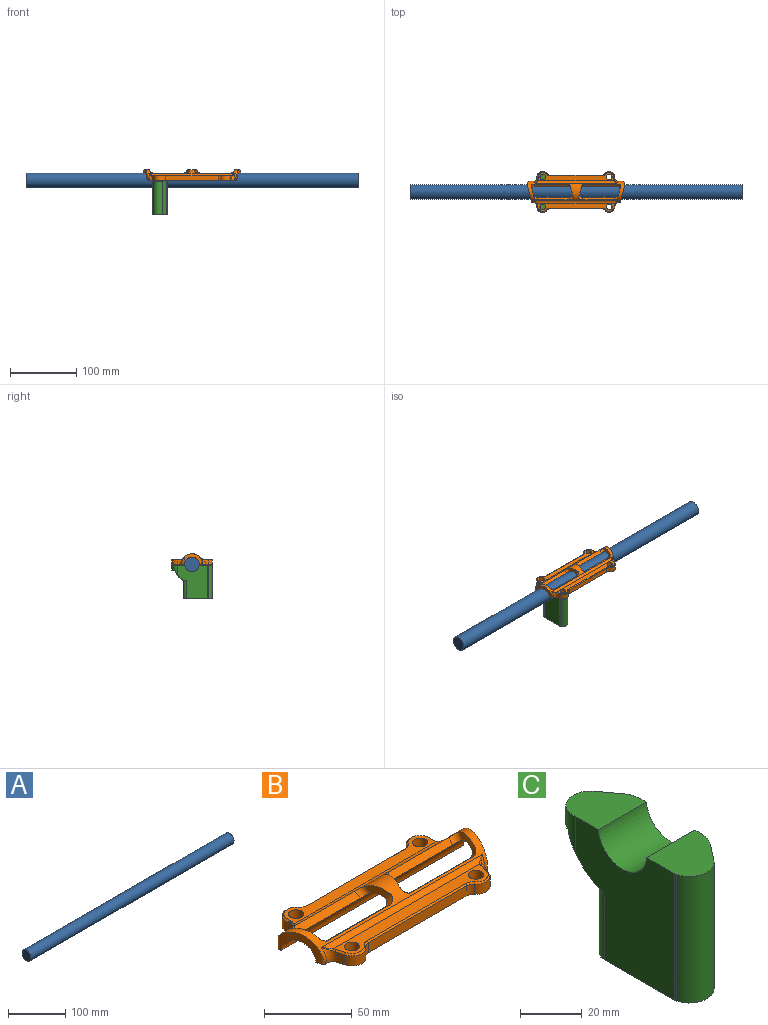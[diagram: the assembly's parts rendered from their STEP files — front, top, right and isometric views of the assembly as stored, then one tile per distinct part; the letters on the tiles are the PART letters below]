
ASSEMBLY  parts=3 mates=2
PART A: 3 faces, bbox 500x22.2x22.2 mm
  f0: cylinder r=11.11mm len=500mm, axis (-1,0,0), area 34910.9mm2, adj f1,f2
  f1: plane 22.23x22.23mm, normal (1,0,0), area 387.9mm2, adj f0
  f2: plane 22.23x22.23mm, normal (-1,0,0), area 387.9mm2, adj f0
PART B: 70 faces, bbox 148.7x62.5x19.9 mm
  f0: plane 147.46x19.58mm, normal (0,0,-1), area 1781.1mm2, adj f1,f2,f3,f4,f5,f25,f26,f29
  f1: cylinder r=11.11mm len=147.22mm, axis (1,0,0), area 2872.5mm2, adj f0,f8,f13,f14,f15,f16,f17,f18
  f2: cylinder r=16.11mm len=147.26mm, axis (1,0,0), area 1271.5mm2, adj f0,f8,f13,f14,f15,f16,f17,f18
  f3: cylinder r=4.3mm len=8.6mm, axis (0,0,-1), area 216.1mm2, adj f0,f6
  f4: plane 78.84x7mm, normal (0,1,0), area 551.9mm2, adj f0,f25,f36,f56
  f5: cylinder r=8mm len=14.51mm, axis (0,0,-1), area 149.8mm2, adj f0,f25,f26,f38
  f6: plane 114.91x12.88mm, normal (0,0,1), area 843.1mm2, adj f3,f22,f36,f37,f38,f39,f41,f66
  f7: plane 118.17x12.87mm, normal (0,0,1), area 893.7mm2, adj f12,f23,f30,f31,f32,f33,f34,f45
  f8: plane 135.5x19.48mm, normal (0,0,-1), area 1770mm2, adj f1,f2,f9,f10,f11,f12,f13,f24
  f9: plane 7x5.95mm, normal (-0.97,-0.26,0), area 37.3mm2, adj f8,f10,f27,f33
  f10: cylinder r=8mm len=14.04mm, axis (0,0,-1), area 124.2mm2, adj f8,f9,f24,f32
  f11: plane 79.49x7mm, normal (0,-1,0), area 556.4mm2, adj f8,f24,f30,f55
  f12: cylinder r=4.3mm len=8.6mm, axis (0,0,-1), area 216.1mm2, adj f7,f8
  f13: plane 26.66x17.58mm, normal (-0.97,-0.26,0), area 167.3mm2, adj f1,f2,f8,f28,f29
  f14: plane 15.6x6.11mm, normal (0.97,0.26,0), area 61.5mm2, adj f1,f2,f18,f19
  f15: plane 50.17x3.72mm, normal (0,-0.67,0.74), area 245.9mm2, adj f1,f2,f18,f21
  f16: plane 15.6x6.11mm, normal (-0.97,-0.26,0), area 61.5mm2, adj f1,f2,f20,f21
  f17: plane 50.17x3.72mm, normal (0,0.67,0.74), area 245.9mm2, adj f1,f2,f19,f20
  f18: cylinder r=5mm len=9.02mm, axis (0.2,-0.73,-0.66), area 47.3mm2, adj f1,f2,f14,f15
  f19: cylinder r=5mm len=8.32mm, axis (0.2,-0.73,0.66), area 36.7mm2, adj f1,f2,f14,f17
  f20: cylinder r=5mm len=9.02mm, axis (-0.2,0.73,-0.66), area 47.3mm2, adj f1,f2,f16,f17
  f21: cylinder r=5mm len=8.32mm, axis (-0.2,0.73,0.66), area 36.7mm2, adj f1,f2,f15,f16
  f22: cylinder r=5mm len=123.2mm, axis (1,0,0), area 540.2mm2, adj f2,f6,f40,f69
  f23: cylinder r=5mm len=130.06mm, axis (1,0,0), area 563.1mm2, adj f2,f7,f35,f65
  f24: cylinder r=5mm len=7mm, axis (0,0,-1), area 31.8mm2, adj f8,f10,f11,f31
  f25: cylinder r=5mm len=7mm, axis (0,0,-1), area 33.3mm2, adj f0,f4,f5,f37
  f26: bspline ~17.25x10.28mm, area 70.5mm2, adj f0,f2,f5,f39,f40
  f27: bspline ~15.58x9.52mm, area 56.6mm2, adj f2,f8,f9,f34,f35
  f28: cylinder r=2.13mm len=6.91mm, axis (0,0,-1), area 9mm2, adj f2,f8,f13
  f29: cylinder r=4.54mm len=12.11mm, axis (0,0,-1), area 47.3mm2, adj f0,f1,f2,f13
  f30: plane 79.49x1mm, normal (0,-0.71,0.71), area 112.4mm2, adj f7,f11,f31,f61
  f31: cone r=6mm half-angle=45deg, axis (0,0,1), area 7.1mm2, adj f7,f24,f30,f32
  f32: cone r=7mm half-angle=45deg, axis (0,0,-1), area 23.5mm2, adj f7,f10,f31,f33
  f33: plane 6.21x2.56mm, normal (-0.68,-0.18,0.71), area 8.7mm2, adj f7,f9,f32,f34
  f34: bspline ~1.99x1.58mm, area 2.3mm2, adj f7,f27,f33,f35
  f35: bspline ~5.95x4.45mm, area 3.4mm2, adj f23,f27,f34
  f36: plane 78.84x1mm, normal (0,0.71,0.71), area 111.5mm2, adj f4,f6,f37,f66
  f37: cone r=6mm half-angle=45deg, axis (0,0,1), area 7.4mm2, adj f6,f25,f36,f38
  f38: cone r=7mm half-angle=45deg, axis (0,0,-1), area 28.9mm2, adj f5,f6,f37,f39
  f39: bspline ~4.47x1.75mm, area 5.5mm2, adj f6,f26,f38,f40
  f40: bspline ~4.37x4.19mm, area 2.5mm2, adj f22,f26,f39
  f41: cylinder r=4.3mm len=8.6mm, axis (0,0,-1), area 216.1mm2, adj f0,f6
  f42: cylinder r=8mm len=14.51mm, axis (0,0,-1), area 149.7mm2, adj f0,f56,f57,f67
  f43: plane 7x5.95mm, normal (0.97,-0.26,0), area 37.3mm2, adj f8,f44,f58,f63
  f44: cylinder r=8mm len=14.04mm, axis (0,0,-1), area 124.2mm2, adj f8,f43,f55,f62
  f45: cylinder r=4.3mm len=8.6mm, axis (0,0,-1), area 216.1mm2, adj f7,f8
  f46: plane 26.66x17.58mm, normal (0.97,-0.26,0), area 167.3mm2, adj f1,f2,f8,f59,f60
  f47: plane 15.6x6.11mm, normal (-0.97,0.26,0), area 61.5mm2, adj f1,f2,f51,f52
  f48: plane 50.17x3.72mm, normal (0,-0.67,0.74), area 245.9mm2, adj f1,f2,f51,f54
  f49: plane 15.6x6.11mm, normal (0.97,-0.26,0), area 61.5mm2, adj f1,f2,f53,f54
  f50: plane 50.17x3.72mm, normal (0,0.67,0.74), area 245.9mm2, adj f1,f2,f52,f53
  f51: cylinder r=5mm len=9.02mm, axis (-0.2,-0.73,-0.66), area 47.3mm2, adj f1,f2,f47,f48
  f52: cylinder r=5mm len=8.32mm, axis (-0.2,-0.73,0.66), area 36.7mm2, adj f1,f2,f47,f50
  f53: cylinder r=5mm len=9.02mm, axis (0.2,0.73,-0.66), area 47.3mm2, adj f1,f2,f49,f50
  f54: cylinder r=5mm len=8.32mm, axis (0.2,0.73,0.66), area 36.7mm2, adj f1,f2,f48,f49
  f55: cylinder r=5mm len=7mm, axis (0,0,-1), area 31.8mm2, adj f8,f11,f44,f61
  f56: cylinder r=5mm len=7mm, axis (0,0,-1), area 33.3mm2, adj f0,f4,f42,f66
  f57: bspline ~17.25x10.28mm, area 70.7mm2, adj f0,f2,f42,f68,f69
  f58: bspline ~15.58x9.52mm, area 56.8mm2, adj f2,f8,f43,f64,f65
  f59: cylinder r=2.13mm len=6.91mm, axis (0,0,-1), area 9mm2, adj f2,f8,f46
  f60: cylinder r=4.54mm len=12.11mm, axis (0,0,-1), area 47.3mm2, adj f0,f1,f2,f46
  f61: cone r=6mm half-angle=45deg, axis (0,0,1), area 7.1mm2, adj f7,f30,f55,f62
  f62: cone r=7mm half-angle=45deg, axis (0,0,-1), area 23.5mm2, adj f7,f44,f61,f63
  f63: plane 6.21x2.56mm, normal (0.68,-0.18,0.71), area 8.7mm2, adj f7,f43,f62,f64
  f64: bspline ~1.99x1.58mm, area 2.4mm2, adj f7,f58,f63,f65
  f65: bspline ~5.95x4.47mm, area 3.5mm2, adj f23,f58,f64
  f66: cone r=6mm half-angle=45deg, axis (0,0,1), area 7.4mm2, adj f6,f36,f56,f67
  f67: cone r=7mm half-angle=45deg, axis (0,0,-1), area 28.9mm2, adj f6,f42,f66,f68
  f68: bspline ~4.47x1.75mm, area 5.6mm2, adj f6,f57,f67,f69
  f69: bspline ~4.37x4.19mm, area 2.5mm2, adj f22,f57,f68
PART C: 25 faces, bbox 22.1x61x50 mm
  f0: cylinder r=8mm len=14.51mm, axis (0,0,1), area 169.2mm2, adj f1,f4,f11,f20,f21
  f1: plane 17.5x7.7mm, normal (0.81,0.59,0), area 115.3mm2, adj f0,f2,f11,f18,f19
  f2: cylinder r=10mm len=21.65mm, axis (0,0,1), area 122.8mm2, adj f1,f5,f11,f17
  f3: plane 21.94x19.43mm, normal (0,0,1), area 344.4mm2, adj f4,f5,f6,f7,f8,f9,f12
  f4: plane 50.01x45.9mm, normal (-1,0,0), area 1702.4mm2, adj f0,f3,f9,f10,f11,f12,f21,f22
  f5: plane 50x27.71mm, normal (1,0,0), area 1073.8mm2, adj f2,f3,f6,f10,f11,f12,f16,f24
  f6: cylinder r=10mm len=50mm, axis (0,0,1), area 330.8mm2, adj f3,f5,f7,f10
  f7: plane 50x7.15mm, normal (0.79,-0.61,0), area 453.2mm2, adj f3,f6,f8,f10
  f8: cylinder r=8mm len=50mm, axis (0,0,1), area 887.3mm2, adj f3,f7,f9,f10
  f9: plane 50x0.85mm, normal (-0.97,-0.26,0), area 43.8mm2, adj f3,f4,f8,f10
  f10: plane 43.91x21.94mm, normal (0,0,-1), area 870.8mm2, adj f4,f5,f6,f7,f8,f9,f14,f23
  f11: plane 21.99x19.43mm, normal (0,0,1), area 341.9mm2, adj f0,f1,f2,f4,f5,f12
  f12: cylinder r=11.11mm len=22.14mm, axis (-1,0,0), area 722.1mm2, adj f3,f4,f5,f11
  f13: plane 12.51x3.76mm, normal (0,0,-1), area 33.3mm2, adj f15,f19,f20
  f14: plane 27.09x11.94mm, normal (0,1,0), area 323.5mm2, adj f10,f15,f23,f24
  f15: cylinder r=27.42mm len=19.94mm, axis (-1,0,0), area 339.9mm2, adj f13,f14,f16,f17,f18,f19,f20,f21
  f16: cone r=26.42mm half-angle=45deg, axis (-1,0,0), area 6.2mm2, adj f5,f15,f17,f24
  f17: bspline ~6x5.03mm, area 9.3mm2, adj f2,f15,f16,f18
  f18: bspline ~11.29x6.7mm, area 12.9mm2, adj f1,f15,f17,f19
  f19: plane 1.93x1.54mm, normal (0.57,0.42,-0.71), area 1.8mm2, adj f1,f13,f15,f18,f20
  f20: cone r=7mm half-angle=45deg, axis (0,0,1), area 22.1mm2, adj f0,f13,f15,f19,f21
  f21: bspline ~9.08x5.75mm, area 9.3mm2, adj f0,f4,f15,f20,f22
  f22: cone r=26.42mm half-angle=45deg, axis (1,0,0), area 22.9mm2, adj f4,f15,f21,f23
  f23: cylinder r=5mm len=27.09mm, axis (0,0,-1), area 206.9mm2, adj f4,f10,f14,f15,f22
  f24: cylinder r=5mm len=27.09mm, axis (0,0,1), area 206.9mm2, adj f5,f10,f14,f15,f16
PLACE A t=(-144.96,100.72,-27.03)mm
PLACE B t=(105.04,100.72,-27.03)mm
PLACE C t=(104.13,100.72,-27.03)mm
MATE cylindrical A.f0 <-> B.f1  axis (-1,0,0) through (105.04,100.72,-27.03)mm
MATE cylindrical C.f12 <-> A.f0  axis (-1,0,0) through (46.18,100.72,-27.03)mm
